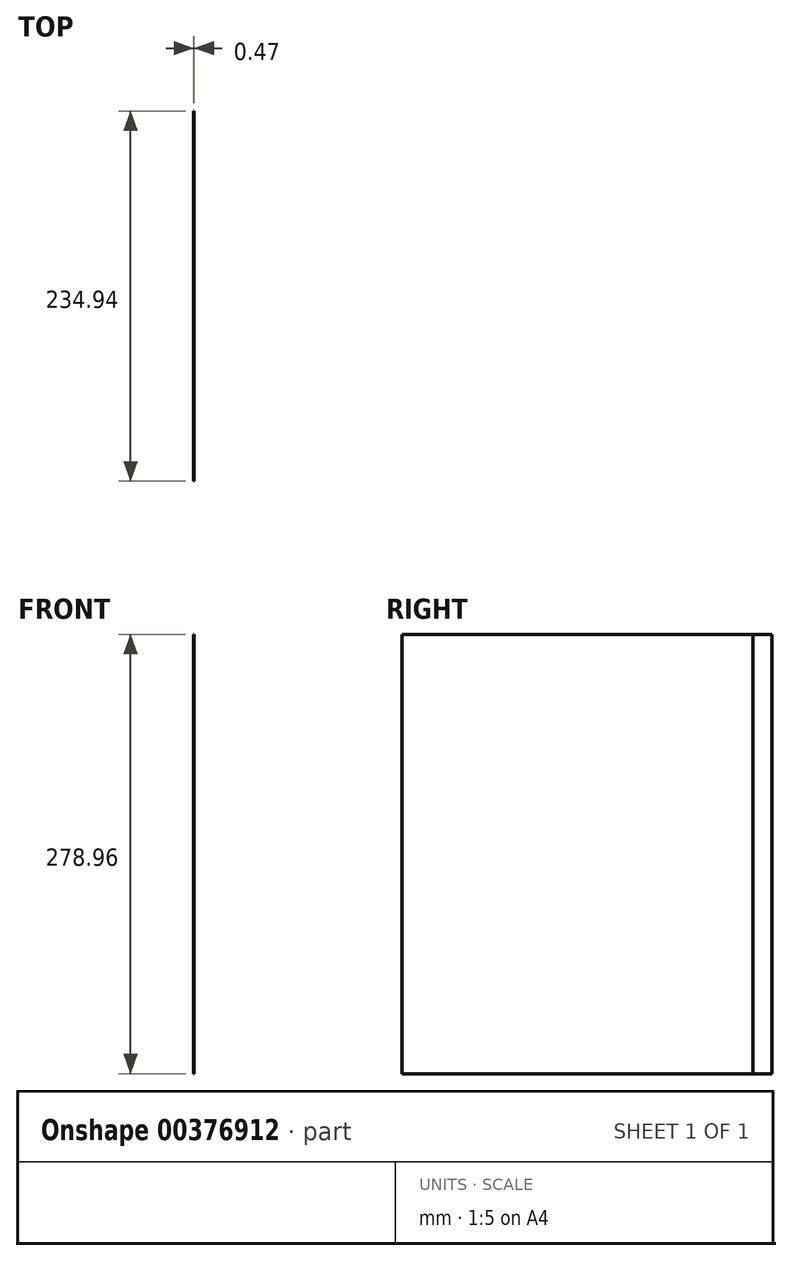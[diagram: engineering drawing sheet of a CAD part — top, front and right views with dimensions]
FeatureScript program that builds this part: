
annotation { "Feature Type Name" : "Feature", "Feature Type Description" : "" }
export const myFeature = defineFeature(function(context is Context, id is Id, definition is map)
    precondition{}
    {
        {
            var Q0;
            Q0=qCreatedBy(makeId("Right.planeOp"),FACE);
            var sketch = newSketch(context, id + "F0", { "sketchPlane" : qUnion([Q0])});
            skLineSegment(sketch, "E0.bottom", {"start": v(117.48, -139.7) * mm, "end": v(-117.47, -139.7) * mm});
            skLineSegment(sketch, "E0.top", {"start": v(117.47, 139.7) * mm, "end": v(-117.47, 139.7) * mm});
            skLineSegment(sketch, "E0.left", {"start": v(117.48, -139.7) * mm, "end": v(117.47, 139.7) * mm});
            skLineSegment(sketch, "E0.right", {"start": v(-117.47, -139.7) * mm, "end": v(-117.47, 139.7) * mm});
            skPoint(sketch, "E0.middle", {"position": v(0, 0) * mm});
            skSolve(sketch);
        }
        {
            assignVariable(context, id + "F1", {"name" : "material", "anyValue" : 0.47});
        }
        {
            var Q0;
            Q0=makeQuery(id+"F0.imprint","IMPRINT",FACE,{"disambiguationData":[TD([[makeQuery(id+"F0.imprint","IMPRINT",EDGE,{"derivedFrom":sQuery(id+"F0.wireOp",EDGE,"E0.bottom")}),-1.0]])]});
            extrude(context, id + "F2", {"entities" : qUnion([Q0]), "depth" : (getVariable(context, 'material')) * mm});
        }
        {
            var Q0;
            Q0=makeQuery(id+"F2.opExtrude","CAP_FACE",FACE,{"disambiguationData":[OSD([sQuery(id+"F0.wireOp",EDGE,"E0.bottom"),sQuery(id+"F0.wireOp",EDGE,"E0.top"),sQuery(id+"F0.wireOp",EDGE,"E0.left"),sQuery(id+"F0.wireOp",EDGE,"E0.right")])],"isStart":false});
            var sketch = newSketch(context, id + "F3", { "sketchPlane" : qUnion([Q0])});
            skLineSegment(sketch, "E1.bottom", {"start": v(117.47, 139.7) * mm, "end": v(105.4, 139.7) * mm});
            skLineSegment(sketch, "E1.top", {"start": v(117.48, -139.7) * mm, "end": v(105.41, -139.7) * mm});
            skLineSegment(sketch, "E1.left", {"start": v(117.47, 139.7) * mm, "end": v(117.48, -139.7) * mm});
            skLineSegment(sketch, "E1.right", {"start": v(105.4, 139.7) * mm, "end": v(105.41, -139.7) * mm});
            skSolve(sketch);
        }
        {
            var Q0;
            Q0 = qSketchRegion(id + "F3", true);
            extrude(context, id + "F4", {"entities" : qUnion([Q0]), "operationType" : NewBodyOperationType.REMOVE, "oppositeDirection" : true, "depth" : (getVariable(context, 'material') / 2) * mm});
        }
        {
            var Q0;
            Q0=makeQuery(id+"F2.opExtrude","SWEPT_FACE",FACE,{"disambiguationData":[OSD([sQuery(id+"F0.wireOp",EDGE,"E0.top")])]});
            extrude(context, id + "F5", {"entities" : qUnion([Q0]), "operationType" : NewBodyOperationType.REMOVE, "oppositeDirection" : true, "depth" : 0.44 * mm});
        }
    });
